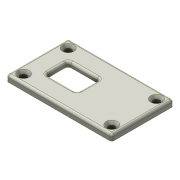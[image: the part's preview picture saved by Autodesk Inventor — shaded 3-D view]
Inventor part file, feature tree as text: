
AUTODESK INVENTOR PART (.ipt)
format: ipt  version: 2021 (Build 250183000, 183)  size: 177,664 bytes
history: native  units: mm
features: sketch x2, other x1, extrude x1, hole x1, fillet x1
ambient origin geometry x8: Origin, YZ Plane, XZ Plane, XY Plane, X Axis, Y Axis, Z Axis, Center Point
bodies: Body1 (feature_tree)
feature tree (6):
  other  "Твердое тело1"
  extrude  "Выдавливание1"  Depth=15.5mm
  hole  "Отверстие1"  [1 undecoded]
  fillet  "Сопряжение5"  Radius=2.5mm
  sketch  "Эскиз1"
  sketch  "Эскиз2"
note: 1 required parameter value undecoded (feature->parameter linkage not recoverable at this tier; creation-order binding heuristic only, values carry confidence <= 0.55)
